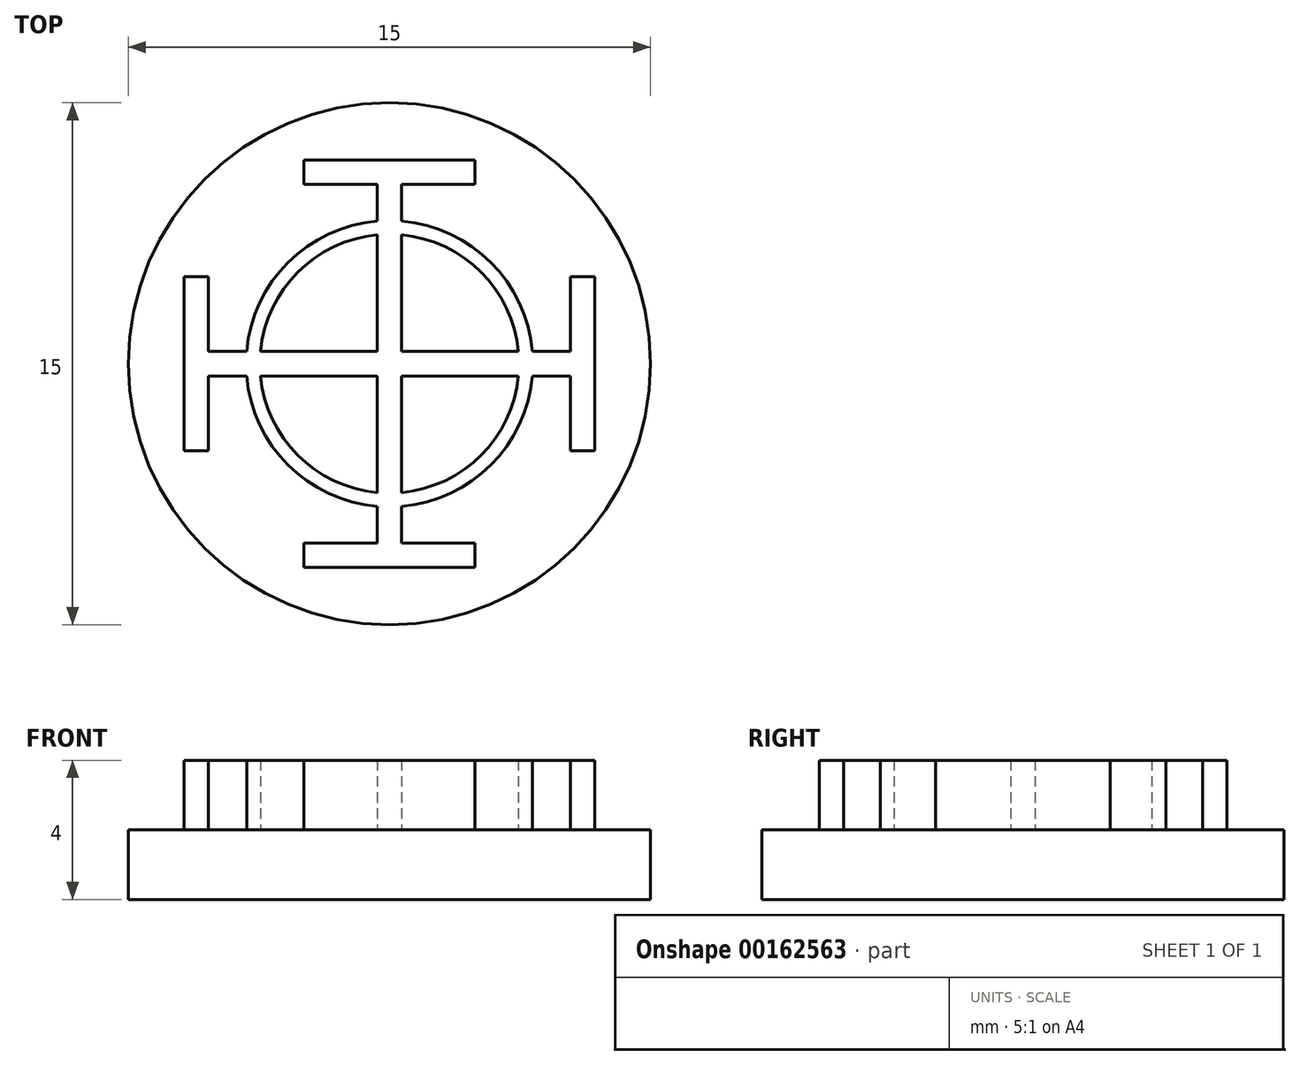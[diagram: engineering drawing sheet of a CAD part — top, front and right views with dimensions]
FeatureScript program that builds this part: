
annotation { "Feature Type Name" : "Feature", "Feature Type Description" : "" }
export const myFeature = defineFeature(function(context is Context, id is Id, definition is map)
    precondition{}
    {
        {
            var Q0;
            Q0=qCreatedBy(makeId("Top.planeOp"),FACE);
            var sketch = newSketch(context, id + "F0", { "sketchPlane" : qUnion([Q0])});
            skCircle(sketch, "E0", {"center": v(0, 0) * mm, "radius": 7.5 * mm});
            skSolve(sketch);
        }
        {
            var Q0;
            Q0 = qSketchRegion(id + "F0", true);
            extrude(context, id + "F1", {"entities" : qUnion([Q0]), "depth" : 2 * mm});
        }
        {
            var Q0;
            Q0=makeQuery(id+"F1.opExtrude","CAP_FACE",FACE,{"disambiguationData":[OSD([sQuery(id+"F0.wireOp",EDGE,"E0")])],"isStart":false});
            var sketch = newSketch(context, id + "F2", { "sketchPlane" : qUnion([Q0])});
            skLineSegment(sketch, "E1.bottom", {"start": v(-2.45, 5.85) * mm, "end": v(0, 5.85) * mm});
            skLineSegment(sketch, "E1.top", {"start": v(-2.45, 5.15) * mm, "end": v(-0.35, 5.15) * mm});
            skLineSegment(sketch, "E1.left", {"start": v(-2.45, 5.85) * mm, "end": v(-2.45, 5.15) * mm});
            skLineSegment(sketch, "E2.bottom", {"start": v(-0.35, 5.85) * mm, "end": v(0, 5.85) * mm});
            skLineSegment(sketch, "E2.left", {"start": v(-0.35, 5.15) * mm, "end": v(-0.35, 4.1) * mm});
            skLineSegment(sketch, "E3.top", {"start": v(-0.35, 0.35) * mm, "end": v(-3.7, 0.35) * mm});
            skLineSegment(sketch, "E4.bottom", {"start": v(-5.9, 2.5) * mm, "end": v(-5.2, 2.5) * mm});
            skLineSegment(sketch, "E4.left", {"start": v(-5.9, 2.5) * mm, "end": v(-5.9, 0) * mm});
            skLineSegment(sketch, "E4.right", {"start": v(-5.2, 2.5) * mm, "end": v(-5.2, 0.35) * mm});
            skPoint(sketch, "E5.orphan", {"position": v(-2.45, 6.6) * mm});
            skArc(sketch, "E6", {"start": v(-0.35, 4.1) * mm, "mid": v(-2.91, 2.91) * mm, "end": v(-4.1, 0.35) * mm});
            skArc(sketch, "E7", {"start": v(-0.35, 3.7) * mm, "mid": v(-2.63, 2.63) * mm, "end": v(-3.7, 0.35) * mm});
            skLineSegment(sketch, "E8.MirrorCS", {"start": v(2.45, 5.85) * mm, "end": v(0, 5.85) * mm});
            skLineSegment(sketch, "E9.MirrorCS", {"start": v(2.45, 5.15) * mm, "end": v(0.35, 5.15) * mm});
            skLineSegment(sketch, "E10.MirrorCS", {"start": v(2.45, 5.85) * mm, "end": v(2.45, 5.15) * mm});
            skLineSegment(sketch, "E11.MirrorCS", {"start": v(0.35, 5.15) * mm, "end": v(0.35, 4.1) * mm});
            skLineSegment(sketch, "E12.MirrorCS", {"start": v(5.9, 2.5) * mm, "end": v(5.9, 0) * mm});
            skLineSegment(sketch, "E13.MirrorCS", {"start": v(5.9, 2.5) * mm, "end": v(5.2, 2.5) * mm});
            skLineSegment(sketch, "E14.MirrorCS", {"start": v(5.2, 2.5) * mm, "end": v(5.2, 0.35) * mm});
            skLineSegment(sketch, "E15.MirrorCS", {"start": v(0.35, 0.35) * mm, "end": v(3.7, 0.35) * mm});
            skLineSegment(sketch, "E16.MirrorCS", {"start": v(-5.9, -2.5) * mm, "end": v(-5.9, 0) * mm});
            skLineSegment(sketch, "E17.MirrorCS", {"start": v(-5.9, -2.5) * mm, "end": v(-5.2, -2.5) * mm});
            skLineSegment(sketch, "E18.MirrorCS", {"start": v(-5.2, -2.5) * mm, "end": v(-5.2, -0.35) * mm});
            skLineSegment(sketch, "E19.MirrorCS", {"start": v(-0.35, -0.35) * mm, "end": v(-3.7, -0.35) * mm});
            skLineSegment(sketch, "E20.MirrorCS", {"start": v(-0.35, -5.15) * mm, "end": v(-0.35, -4.1) * mm});
            skLineSegment(sketch, "E21.MirrorCS", {"start": v(-2.45, -5.15) * mm, "end": v(-0.35, -5.15) * mm});
            skLineSegment(sketch, "E22.MirrorCS", {"start": v(-2.45, -5.85) * mm, "end": v(0, -5.85) * mm});
            skLineSegment(sketch, "E23.MirrorCS", {"start": v(-2.45, -5.85) * mm, "end": v(-2.45, -5.15) * mm});
            skLineSegment(sketch, "E24.MirrorCS", {"start": v(2.45, -5.85) * mm, "end": v(0, -5.85) * mm});
            skLineSegment(sketch, "E25.MirrorCS", {"start": v(2.45, -5.15) * mm, "end": v(0.35, -5.15) * mm});
            skLineSegment(sketch, "E26.MirrorCS", {"start": v(2.45, -5.85) * mm, "end": v(2.45, -5.15) * mm});
            skLineSegment(sketch, "E27.MirrorCS", {"start": v(0.35, -5.15) * mm, "end": v(0.35, -4.1) * mm});
            skLineSegment(sketch, "E28.MirrorCS", {"start": v(0.35, -0.35) * mm, "end": v(3.7, -0.35) * mm});
            skLineSegment(sketch, "E29.MirrorCS", {"start": v(5.2, -2.5) * mm, "end": v(5.2, -0.35) * mm});
            skLineSegment(sketch, "E30.MirrorCS", {"start": v(5.9, -2.5) * mm, "end": v(5.2, -2.5) * mm});
            skLineSegment(sketch, "E31.MirrorCS", {"start": v(5.9, -2.5) * mm, "end": v(5.9, 0) * mm});
            skPoint(sketch, "E32.orphan", {"position": v(0.35, 5.85) * mm});
            skPoint(sketch, "E33.orphan", {"position": v(0, 5.15) * mm});
            skPoint(sketch, "E34.orphan", {"position": v(-5.2, 0) * mm});
            skPoint(sketch, "E35.start.orphan", {"position": v(0, 10.5) * mm});
            skPoint(sketch, "E36.orphan", {"position": v(-11.6, 0) * mm});
            skArc(sketch, "E37.trimOffspring", {"start": v(-4.1, -0.35) * mm, "mid": v(-2.91, -2.91) * mm, "end": v(-0.35, -4.1) * mm});
            skArc(sketch, "E38.trimOffspring", {"start": v(-3.7, -0.35) * mm, "mid": v(-2.63, -2.63) * mm, "end": v(-0.35, -3.7) * mm});
            skLineSegment(sketch, "E39.trimOffspring", {"start": v(-4.1, -0.35) * mm, "end": v(-5.2, -0.35) * mm});
            skLineSegment(sketch, "E40.trimOffspring", {"start": v(-4.1, 0.35) * mm, "end": v(-5.2, 0.35) * mm});
            skLineSegment(sketch, "E41.trimOffspring", {"start": v(-0.35, 3.7) * mm, "end": v(-0.35, 0.35) * mm});
            skLineSegment(sketch, "E42.trimOffspring", {"start": v(0.35, 3.7) * mm, "end": v(0.35, 0.35) * mm});
            skArc(sketch, "E43.trimOffspring", {"start": v(3.7, 0.35) * mm, "mid": v(2.63, 2.63) * mm, "end": v(0.35, 3.7) * mm});
            skLineSegment(sketch, "E44.trimOffspring", {"start": v(4.1, 0.35) * mm, "end": v(5.2, 0.35) * mm});
            skArc(sketch, "E45.trimOffspring", {"start": v(4.1, 0.35) * mm, "mid": v(2.91, 2.91) * mm, "end": v(0.35, 4.1) * mm});
            skLineSegment(sketch, "E46.trimOffspring", {"start": v(4.1, -0.35) * mm, "end": v(5.2, -0.35) * mm});
            skLineSegment(sketch, "E47.trimOffspring", {"start": v(-0.35, -3.7) * mm, "end": v(-0.35, -0.35) * mm});
            skLineSegment(sketch, "E48.trimOffspring", {"start": v(0.35, -3.7) * mm, "end": v(0.35, -0.35) * mm});
            skArc(sketch, "E49.trimOffspring", {"start": v(0.35, -3.7) * mm, "mid": v(2.63, -2.63) * mm, "end": v(3.7, -0.35) * mm});
            skArc(sketch, "E50.trimOffspring", {"start": v(0.35, -4.1) * mm, "mid": v(2.91, -2.91) * mm, "end": v(4.1, -0.35) * mm});
            skSolve(sketch);
        }
        {
            var Q0;
            Q0 = qSketchRegion(id + "F2", true);
            extrude(context, id + "F3", {"entities" : qUnion([Q0]), "operationType" : NewBodyOperationType.ADD, "depth" : 2 * mm});
        }
    });
